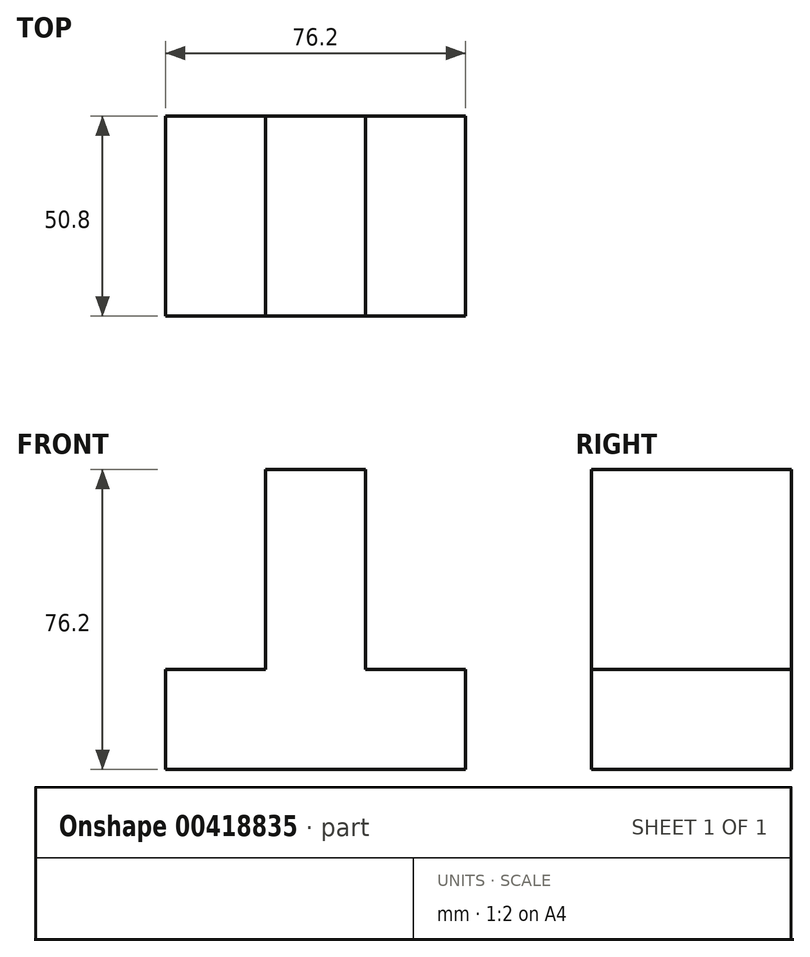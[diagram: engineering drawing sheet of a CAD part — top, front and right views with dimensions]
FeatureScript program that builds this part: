
annotation { "Feature Type Name" : "Feature", "Feature Type Description" : "" }
export const myFeature = defineFeature(function(context is Context, id is Id, definition is map)
    precondition{}
    {
        {
            var Q0;
            Q0=qCreatedBy(makeId("Front.planeOp"),FACE);
            var sketch = newSketch(context, id + "F0", { "sketchPlane" : qUnion([Q0])});
            skLineSegment(sketch, "E0", {"start": v(0, 0) * mm, "end": v(-76.2, 0) * mm});
            skLineSegment(sketch, "E1", {"start": v(-76.2, 0) * mm, "end": v(-76.2, 25.4) * mm});
            skLineSegment(sketch, "E2", {"start": v(0, 0) * mm, "end": v(0, 25.4) * mm});
            skLineSegment(sketch, "E3", {"start": v(-76.2, 25.4) * mm, "end": v(-50.8, 25.4) * mm});
            skLineSegment(sketch, "E4", {"start": v(0, 25.4) * mm, "end": v(-25.4, 25.4) * mm});
            skLineSegment(sketch, "E5", {"start": v(-50.8, 25.4) * mm, "end": v(-50.8, 76.2) * mm});
            skLineSegment(sketch, "E6", {"start": v(-25.4, 25.4) * mm, "end": v(-25.4, 76.2) * mm});
            skLineSegment(sketch, "E7", {"start": v(-50.8, 76.2) * mm, "end": v(-25.4, 76.2) * mm});
            skSolve(sketch);
        }
        {
            var Q0;
            Q0 = qSketchRegion(id + "F0", true);
            extrude(context, id + "F1", {"entities" : qUnion([Q0]), "depth" : 50.8 * mm});
        }
    });
